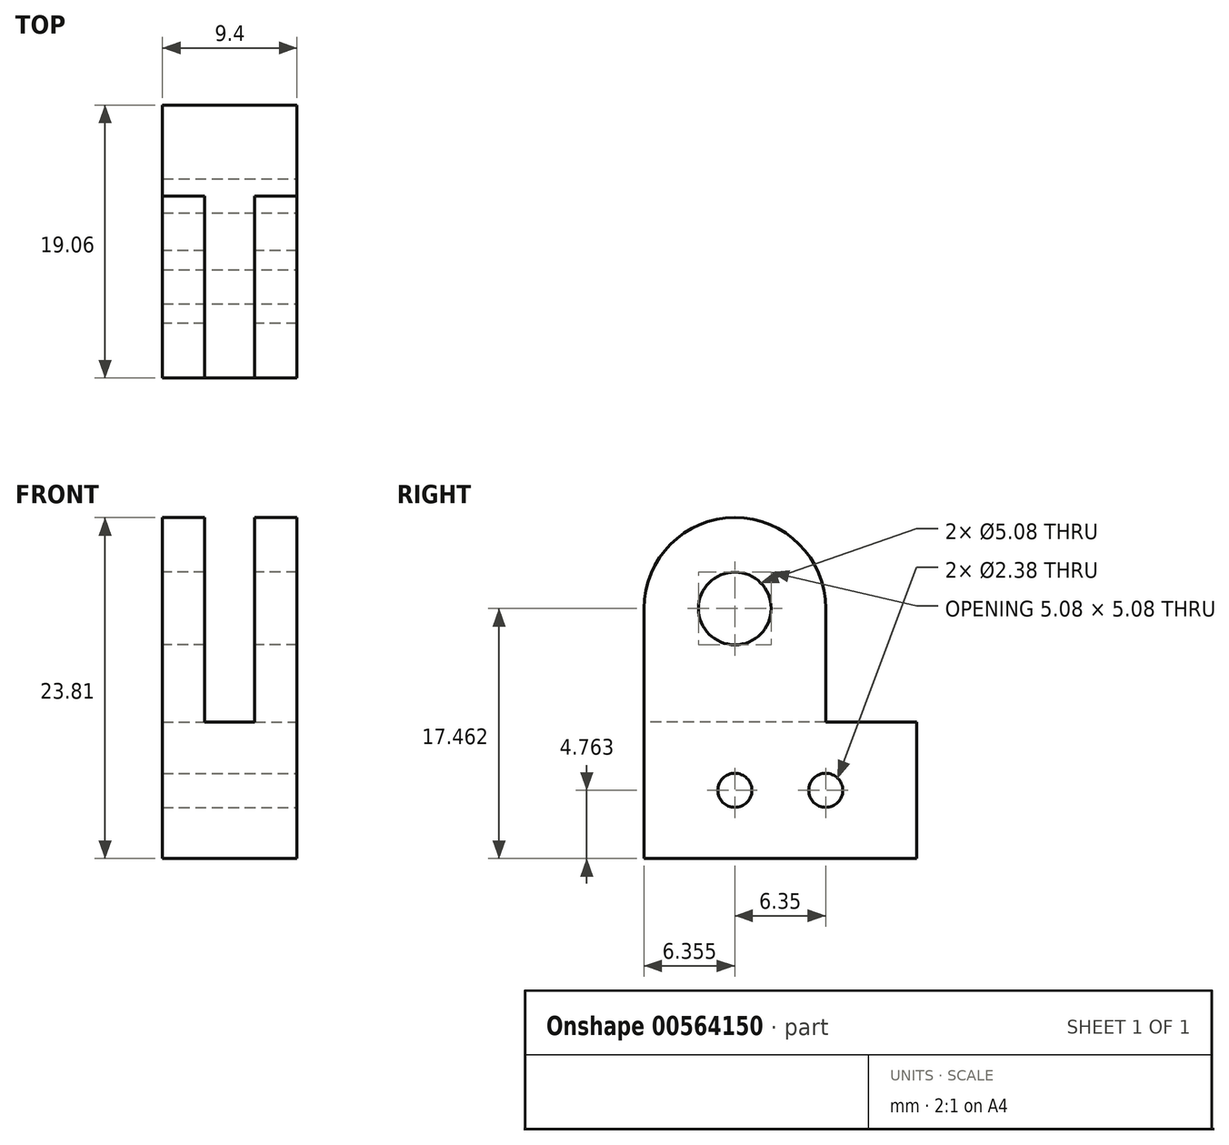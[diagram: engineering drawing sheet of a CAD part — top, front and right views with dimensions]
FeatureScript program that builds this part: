
annotation { "Feature Type Name" : "Feature", "Feature Type Description" : "" }
export const myFeature = defineFeature(function(context is Context, id is Id, definition is map)
    precondition{}
    {
        {
            var Q0;
            Q0=qCreatedBy(makeId("Right.planeOp"),FACE);
            var sketch = newSketch(context, id + "F0", { "sketchPlane" : qUnion([Q0])});
            skLineSegment(sketch, "E0.bottom", {"start": v(9.53, 0) * mm, "end": v(-9.52, 0) * mm});
            skLineSegment(sketch, "E0.top", {"start": v(9.53, 9.52) * mm, "end": v(-9.52, 9.52) * mm});
            skLineSegment(sketch, "E0.left", {"start": v(9.53, 0) * mm, "end": v(9.53, 9.52) * mm});
            skLineSegment(sketch, "E0.right", {"start": v(-9.52, 0) * mm, "end": v(-9.52, 9.52) * mm});
            skPoint(sketch, "E1", {"position": v(0, 0) * mm});
            skSolve(sketch);
        }
        {
            var Q0;
            Q0=qSketchRegion(id+"F0",true);
            extrude(context, id + "F1", {"entities" : qUnion([Q0]), "endBound" : BoundingType.SYMMETRIC, "depth" : 9.4 * mm, "offsetDistance" : 25.4 * mm});
        }
        {
            var Q0;
            Q0=qCreatedBy(makeId("Right.planeOp"),FACE);
            var sketch = newSketch(context, id + "F2", { "sketchPlane" : qUnion([Q0])});
            skCircle(sketch, "E2", {"center": v(-3.17, 17.46) * mm, "radius": 6.35 * mm});
            skCircle(sketch, "E3", {"center": v(-3.17, 17.46) * mm, "radius": 2.54 * mm});
            skLineSegment(sketch, "E4", {"start": v(-10.81, 0) * mm, "end": v(-10.81, 9.53) * mm});
            skPoint(sketch, "E5", {"position": v(-10.81, 4.76) * mm});
            skLineSegment(sketch, "E6", {"start": v(-9.52, 0) * mm, "end": v(-9.52, 17.46) * mm});
            skLineSegment(sketch, "E7", {"start": v(3.18, 17.46) * mm, "end": v(3.18, 0) * mm});
            skLineSegment(sketch, "E8", {"start": v(3.18, 0) * mm, "end": v(-9.52, 0) * mm});
            skSolve(sketch);
        }
        {
            var Q0;
            Q0=qSketchRegion(id+"F2",true);
            extrude(context, id + "F3", {"entities" : qUnion([Q0]), "operationType" : NewBodyOperationType.ADD, "endBound" : BoundingType.SYMMETRIC, "depth" : 9.4 * mm, "offsetDistance" : 25.4 * mm});
        }
        {
            var Q0;
            Q0=makeQuery(id+"F1.opExtrude","CAP_FACE",FACE,{"disambiguationData":[OSD([sQuery(id+"F0.wireOp",EDGE,"E0.bottom"),sQuery(id+"F0.wireOp",EDGE,"E0.top"),sQuery(id+"F0.wireOp",EDGE,"E0.left"),sQuery(id+"F0.wireOp",EDGE,"E0.right")])],"isStart":false});
            var sketch = newSketch(context, id + "F4", { "sketchPlane" : qUnion([Q0])});
            skCircle(sketch, "E9", {"center": v(-3.17, 4.76) * mm, "radius": 1.2 * mm});
            skCircle(sketch, "E10.MirrorC", {"center": v(3.18, 4.76) * mm, "radius": 1.2 * mm});
            skPoint(sketch, "E11", {"position": v(-9.52, 8.73) * mm});
            skSolve(sketch);
        }
        {
            var Q0;
            Q0=qSketchRegion(id+"F4",true);
            extrude(context, id + "F5", {"entities" : qUnion([Q0]), "operationType" : NewBodyOperationType.REMOVE, "endBound" : BoundingType.THROUGH_ALL, "oppositeDirection" : true, "depth" : 25.4 * mm, "offsetDistance" : 25.4 * mm});
        }
        {
            var Q0;
            Q0=makeQuery(id+"F3.boolean.opBoolean","MERGE",FACE,{"derivedFrom":[makeQuery(id+"F1.opExtrude","SWEPT_FACE",FACE,{"disambiguationData":[OSD([sQuery(id+"F0.wireOp",EDGE,"E0.right")])]}),makeQuery(id+"F3.opExtrude","SWEPT_FACE",FACE,{"disambiguationData":[OSD([sQuery(id+"F2.wireOp",EDGE,"E6")])]})]});
            var sketch = newSketch(context, id + "F6", { "sketchPlane" : qUnion([Q0])});
            skLineSegment(sketch, "E12", {"start": v(-4.7, 19.05) * mm, "end": v(4.7, 19.05) * mm});
            skLineSegment(sketch, "E13.bottom", {"start": v(-1.75, 28.57) * mm, "end": v(1.75, 28.57) * mm});
            skLineSegment(sketch, "E13.top", {"start": v(-1.75, 9.52) * mm, "end": v(1.75, 9.52) * mm});
            skLineSegment(sketch, "E13.left", {"start": v(1.75, 28.57) * mm, "end": v(1.75, 9.52) * mm});
            skLineSegment(sketch, "E13.right", {"start": v(-1.75, 28.57) * mm, "end": v(-1.75, 9.52) * mm});
            skPoint(sketch, "E13.middle", {"position": v(0, 19.05) * mm});
            skSolve(sketch);
        }
        {
            var Q0;
            Q0 = qSketchRegion(id + "F6", true);
            extrude(context, id + "F7", {"entities" : qUnion([Q0]), "operationType" : NewBodyOperationType.REMOVE, "endBound" : BoundingType.THROUGH_ALL, "oppositeDirection" : true, "depth" : 25.4 * mm, "offsetDistance" : 25.4 * mm});
        }
    });
